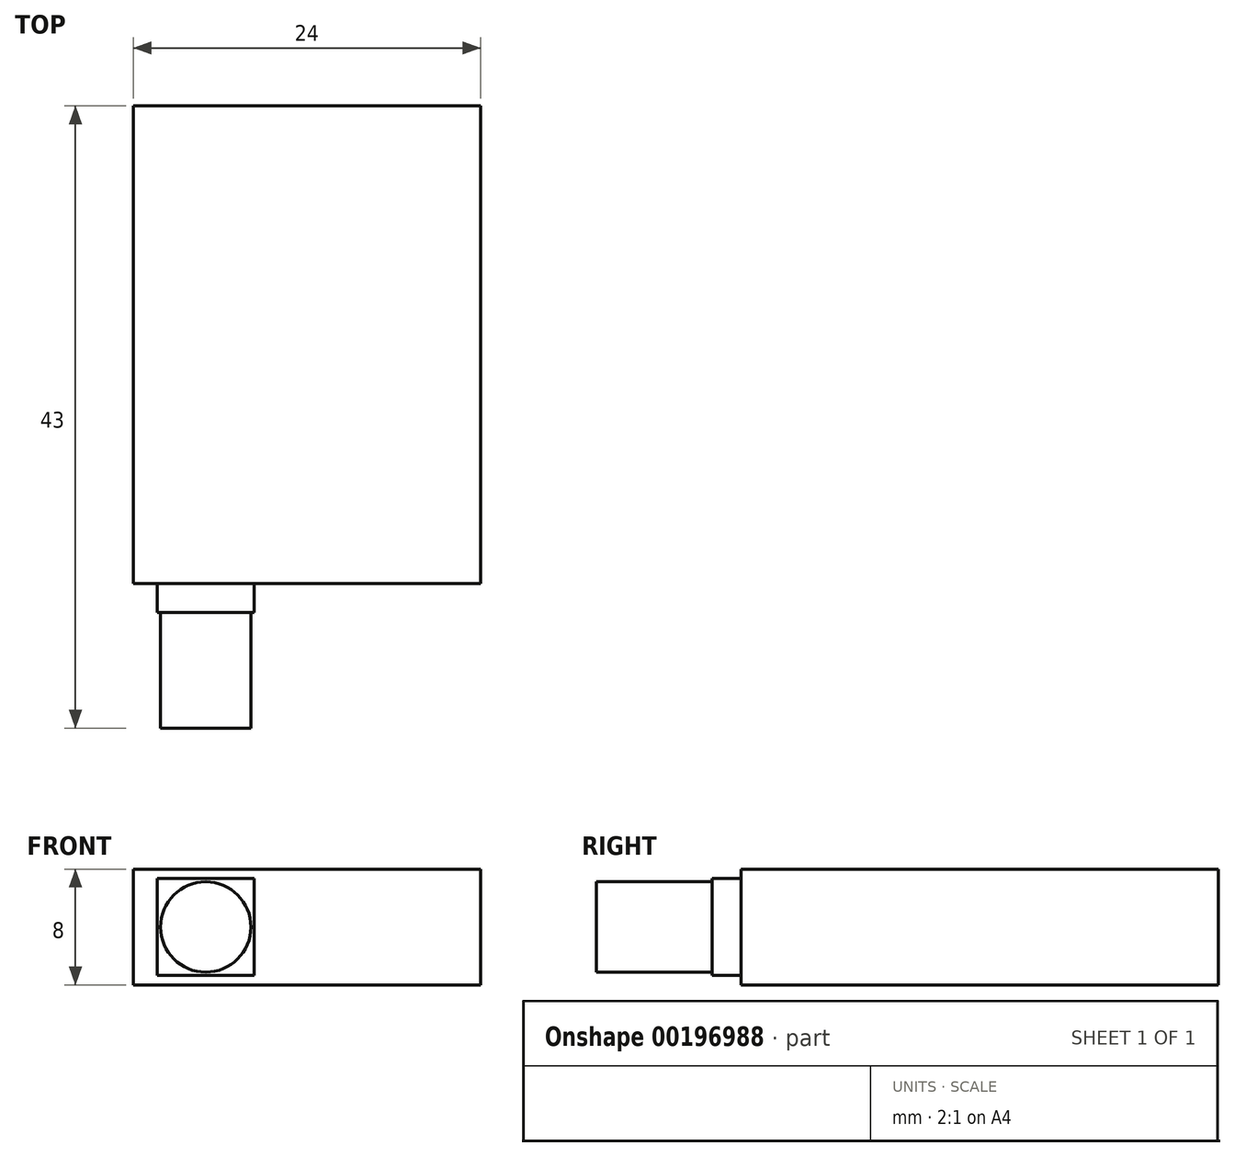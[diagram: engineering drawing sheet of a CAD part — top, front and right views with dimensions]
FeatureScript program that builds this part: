
annotation { "Feature Type Name" : "Feature", "Feature Type Description" : "" }
export const myFeature = defineFeature(function(context is Context, id is Id, definition is map)
    precondition{}
    {
        {
            var Q0;
            Q0=qCreatedBy(makeId("Top.planeOp"),FACE);
            var sketch = newSketch(context, id + "F0", { "sketchPlane" : qUnion([Q0])});
            skLineSegment(sketch, "E0.bottom", {"start": v(12, 16.5) * mm, "end": v(-12, 16.5) * mm});
            skLineSegment(sketch, "E0.top", {"start": v(12, -16.5) * mm, "end": v(-12, -16.5) * mm});
            skLineSegment(sketch, "E0.left", {"start": v(12, 16.5) * mm, "end": v(12, -16.5) * mm});
            skLineSegment(sketch, "E0.right", {"start": v(-12, 16.5) * mm, "end": v(-12, -16.5) * mm});
            skPoint(sketch, "E0.middle", {"position": v(0, 0) * mm});
            skSolve(sketch);
        }
        {
            var Q0;
            Q0 = qSketchRegion(id + "F0", true);
            extrude(context, id + "F1", {"entities" : qUnion([Q0]), "depth" : 8 * mm});
        }
        {
            var Q0;
            Q0=makeQuery(id+"F1.opExtrude","SWEPT_FACE",FACE,{"disambiguationData":[OSD([sQuery(id+"F0.wireOp",EDGE,"E0.top")])]});
            var sketch = newSketch(context, id + "F2", { "sketchPlane" : qUnion([Q0])});
            skLineSegment(sketch, "E1.bottom", {"start": v(-3.65, 0.65) * mm, "end": v(-10.35, 0.65) * mm});
            skLineSegment(sketch, "E1.top", {"start": v(-3.65, 7.35) * mm, "end": v(-10.35, 7.35) * mm});
            skLineSegment(sketch, "E1.left", {"start": v(-3.65, 0.65) * mm, "end": v(-3.65, 7.35) * mm});
            skLineSegment(sketch, "E1.right", {"start": v(-10.35, 0.65) * mm, "end": v(-10.35, 7.35) * mm});
            skPoint(sketch, "E1.middle", {"position": v(-7, 4) * mm});
            skLineSegment(sketch, "E2", {"start": v(-12, 4) * mm, "end": v(-7, 4) * mm, "construction": true});
            skSolve(sketch);
        }
        {
            var Q0;
            Q0 = qSketchRegion(id + "F2", true);
            extrude(context, id + "F3", {"entities" : qUnion([Q0]), "operationType" : NewBodyOperationType.ADD, "depth" : 2 * mm});
        }
        {
            var Q0;
            Q0=makeQuery(id+"F3.opExtrude","CAP_FACE",FACE,{"disambiguationData":[OSD([sQuery(id+"F2.wireOp",EDGE,"E1.bottom"),sQuery(id+"F2.wireOp",EDGE,"E1.top"),sQuery(id+"F2.wireOp",EDGE,"E1.left"),sQuery(id+"F2.wireOp",EDGE,"E1.right")])],"isStart":false});
            var sketch = newSketch(context, id + "F4", { "sketchPlane" : qUnion([Q0])});
            skLineSegment(sketch, "E3", {"start": v(-10.35, 7.35) * mm, "end": v(-3.65, 0.65) * mm, "construction": true});
            skCircle(sketch, "E4", {"center": v(-7, 4) * mm, "radius": 3.12 * mm});
            skSolve(sketch);
        }
        {
            var Q0;
            Q0 = qSketchRegion(id + "F4", true);
            extrude(context, id + "F5", {"entities" : qUnion([Q0]), "operationType" : NewBodyOperationType.ADD, "depth" : 8 * mm});
        }
    });
